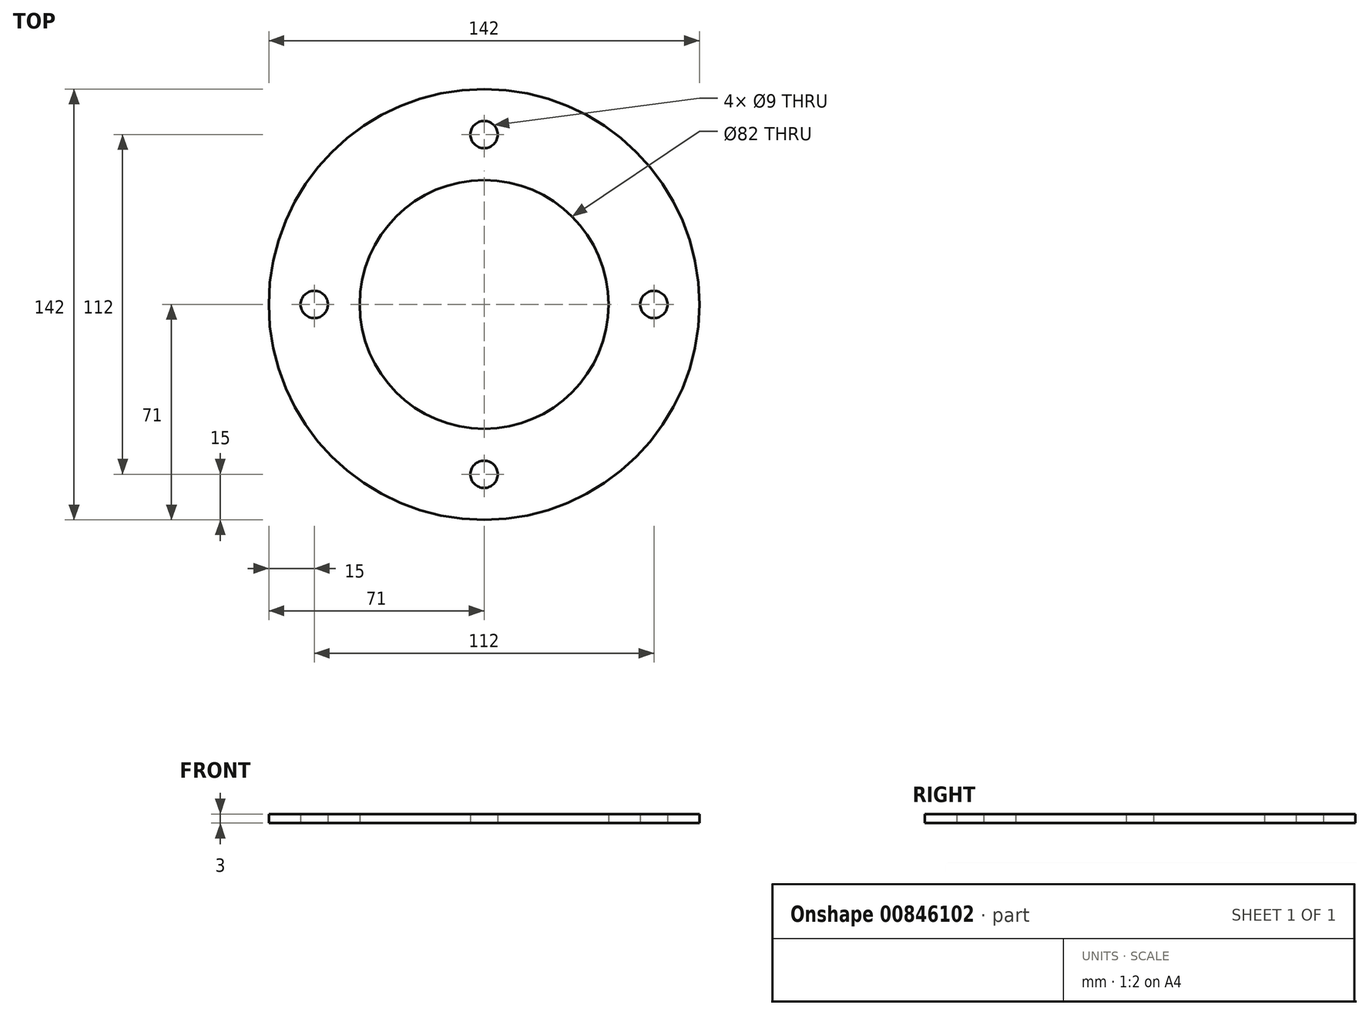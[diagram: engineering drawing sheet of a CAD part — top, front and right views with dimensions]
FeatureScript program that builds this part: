
annotation { "Feature Type Name" : "Feature", "Feature Type Description" : "" }
export const myFeature = defineFeature(function(context is Context, id is Id, definition is map)
    precondition{}
    {
        {
            var Q0;
            Q0=qCreatedBy(makeId("Top.planeOp"),FACE);
            var sketch = newSketch(context, id + "F0", { "sketchPlane" : qUnion([Q0])});
            skCircle(sketch, "E0", {"center": v(0, 0) * mm, "radius": 41 * mm});
            skCircle(sketch, "E1", {"center": v(0, 0) * mm, "radius": 71 * mm});
            skCircle(sketch, "E2", {"center": v(0, 56) * mm, "radius": 4.5 * mm});
            skCircle(sketch, "E3.1.0", {"center": v(-56, 0) * mm, "radius": 4.5 * mm});
            skCircle(sketch, "E3.2.0", {"center": v(0, -56) * mm, "radius": 4.5 * mm});
            skCircle(sketch, "E3.3.0", {"center": v(56, 0) * mm, "radius": 4.5 * mm});
            skSolve(sketch);
        }
        {
            var Q0;
            Q0=makeQuery(id+"F0.imprint","IMPRINT",FACE,{"disambiguationData":[TD([[makeQuery(id+"F0.imprint","IMPRINT",EDGE,{"derivedFrom":sQuery(id+"F0.wireOp",EDGE,"E0")}),-1.0]])]});
            extrude(context, id + "F1", {"entities" : qUnion([Q0]), "depth" : 3 * mm, "offsetDistance" : 25 * mm});
        }
    });
